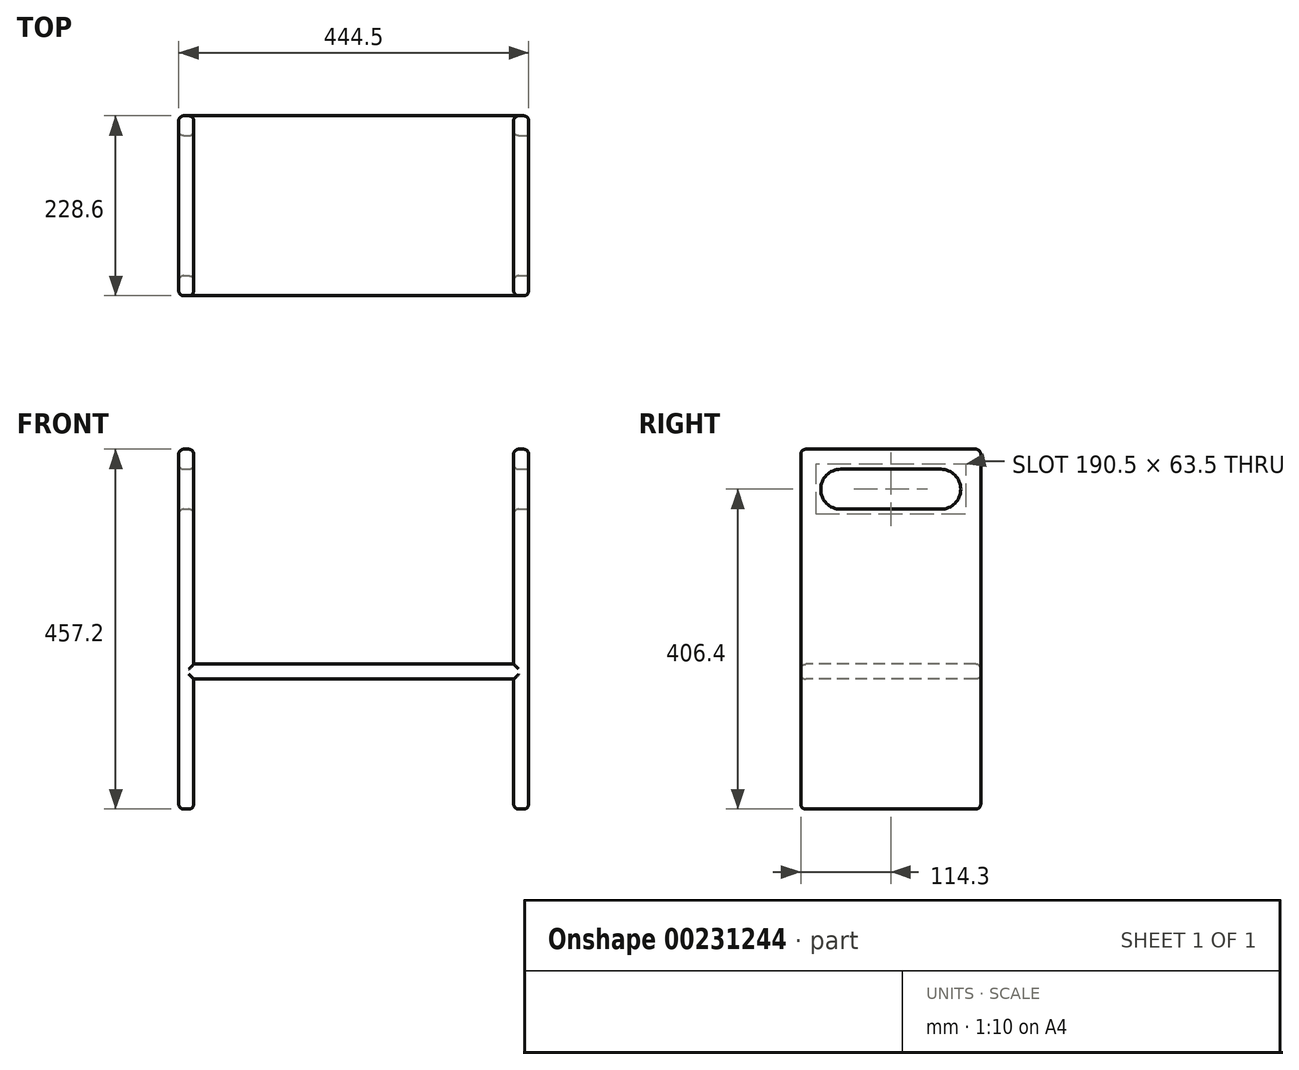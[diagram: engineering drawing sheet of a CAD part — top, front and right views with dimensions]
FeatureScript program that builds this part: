
annotation { "Feature Type Name" : "Feature", "Feature Type Description" : "" }
export const myFeature = defineFeature(function(context is Context, id is Id, definition is map)
    precondition{}
    {
        {
            var Q0;
            Q0=qCreatedBy(makeId("Top.planeOp"),FACE);
            var sketch = newSketch(context, id + "F0", { "sketchPlane" : qUnion([Q0])});
            skLineSegment(sketch, "E0.bottom", {"start": v(-209.55, 114.3) * mm, "end": v(209.55, 114.3) * mm});
            skLineSegment(sketch, "E0.top", {"start": v(-209.55, -114.3) * mm, "end": v(209.55, -114.3) * mm});
            skLineSegment(sketch, "E0.left", {"start": v(-209.55, 114.3) * mm, "end": v(-209.55, -114.3) * mm});
            skLineSegment(sketch, "E0.right", {"start": v(209.55, 114.3) * mm, "end": v(209.55, -114.3) * mm});
            skPoint(sketch, "E0.middle", {"position": v(0, 0) * mm});
            skSolve(sketch);
        }
        {
            var Q0;
            Q0 = qSketchRegion(id + "F0", true);
            extrude(context, id + "F1", {"entities" : qUnion([Q0]), "depth" : 19.05 * mm});
        }
        {
            var Q0;
            Q0=makeQuery(id+"F1.opExtrude","SWEPT_FACE",FACE,{"disambiguationData":[OSD([sQuery(id+"F0.wireOp",EDGE,"E0.top")])]});
            var sketch = newSketch(context, id + "F2", { "sketchPlane" : qUnion([Q0])});
            skLineSegment(sketch, "E1.bottom", {"start": v(203.2, -165.1) * mm, "end": v(222.25, -165.1) * mm});
            skLineSegment(sketch, "E1.top", {"start": v(203.2, 292.1) * mm, "end": v(222.25, 292.1) * mm});
            skLineSegment(sketch, "E1.left", {"start": v(203.2, -165.1) * mm, "end": v(203.2, 0) * mm});
            skLineSegment(sketch, "E1.right", {"start": v(222.25, -165.1) * mm, "end": v(222.25, 292.1) * mm});
            skPoint(sketch, "E1.middle", {"position": v(212.73, 63.5) * mm});
            skLineSegment(sketch, "E2.bottom", {"start": v(203.2, 19.05) * mm, "end": v(209.55, 19.05) * mm});
            skLineSegment(sketch, "E2.top", {"start": v(203.2, 0) * mm, "end": v(209.55, 0) * mm});
            skLineSegment(sketch, "E2.right", {"start": v(209.55, 19.05) * mm, "end": v(209.55, 0) * mm});
            skLineSegment(sketch, "E3.trimOffspring", {"start": v(203.2, 19.05) * mm, "end": v(203.2, 292.1) * mm});
            skLineSegment(sketch, "E4.MirrorCS", {"start": v(-203.2, 292.1) * mm, "end": v(-222.25, 292.1) * mm});
            skLineSegment(sketch, "E5.MirrorCS", {"start": v(-203.2, 19.05) * mm, "end": v(-203.2, 292.1) * mm});
            skLineSegment(sketch, "E6.MirrorCS", {"start": v(-222.25, -165.1) * mm, "end": v(-222.25, 292.1) * mm});
            skLineSegment(sketch, "E7.MirrorCS", {"start": v(-203.2, 19.05) * mm, "end": v(-209.55, 19.05) * mm});
            skLineSegment(sketch, "E8.MirrorCS", {"start": v(-209.55, 19.05) * mm, "end": v(-209.55, 0) * mm});
            skLineSegment(sketch, "E9.MirrorCS", {"start": v(-203.2, 0) * mm, "end": v(-209.55, 0) * mm});
            skLineSegment(sketch, "E10.MirrorCS", {"start": v(-203.2, -165.1) * mm, "end": v(-203.2, 0) * mm});
            skLineSegment(sketch, "E11.MirrorCS", {"start": v(-203.2, -165.1) * mm, "end": v(-222.25, -165.1) * mm});
            skSolve(sketch);
        }
        {
            var Q0;
            Q0 = qSketchRegion(id + "F2", true);
            var Q1;
            Q1=makeQuery(id+"F1.opExtrude","SWEPT_FACE",FACE,{"disambiguationData":[OSD([sQuery(id+"F0.wireOp",EDGE,"E0.bottom")])]});
            extrude(context, id + "F3", {"entities" : qUnion([Q0]), "operationType" : NewBodyOperationType.ADD, "endBound" : BoundingType.UP_TO_SURFACE, "oppositeDirection" : true, "endBoundEntityFace" : qUnion([Q1]), "depth" : 25.4 * mm});
        }
        {
            var Q0;
            Q0=makeQuery(id+"F3.opExtrude","SWEPT_FACE",FACE,{"disambiguationData":[OSD([sQuery(id+"F2.wireOp",EDGE,"E1.right")])]});
            var sketch = newSketch(context, id + "F4", { "sketchPlane" : qUnion([Q0])});
            skLineSegment(sketch, "E12", {"start": v(-63.5, 241.3) * mm, "end": v(63.5, 241.3) * mm, "construction": true});
            skArc(sketch, "E13", {"start": v(-63.5, 266.7) * mm, "mid": v(-88.9, 241.3) * mm, "end": v(-63.5, 215.9) * mm});
            skArc(sketch, "E14", {"start": v(63.5, 215.9) * mm, "mid": v(88.9, 241.3) * mm, "end": v(63.5, 266.7) * mm});
            skLineSegment(sketch, "E15", {"start": v(-63.5, 266.7) * mm, "end": v(63.5, 266.7) * mm});
            skLineSegment(sketch, "E16", {"start": v(-63.5, 215.9) * mm, "end": v(63.5, 215.9) * mm});
            skSolve(sketch);
        }
        {
            var Q0;
            Q0 = qSketchRegion(id + "F4", true);
            extrude(context, id + "F5", {"entities" : qUnion([Q0]), "operationType" : NewBodyOperationType.REMOVE, "endBound" : BoundingType.THROUGH_ALL, "oppositeDirection" : true, "depth" : 25.4 * mm});
        }
        {
            var Q0;
            Q0=makeQuery(id+"F5.boolean.opBoolean","COPY",EDGE,{"derivedFrom":makeQuery(id+"F5.opExtrude","CAP_EDGE",EDGE,{"disambiguationData":[OSD([sQuery(id+"F4.wireOp",EDGE,"E16")])],"isStart":true})});
            var Q1;
            Q1=makeQuery(id+"F5.boolean.opBoolean","INTERSECT",EDGE,{"derivedFrom":[makeQuery(id+"F3.opExtrude","SWEPT_FACE",FACE,{"disambiguationData":[OSD([sQuery(id+"F2.wireOp",EDGE,"E5.MirrorCS")])]}),makeQuery(id+"F5.opExtrude","SWEPT_FACE",FACE,{"disambiguationData":[OSD([sQuery(id+"F4.wireOp",EDGE,"E16")])]})]});
            var Q2;
            Q2=makeQuery(id+"F5.boolean.opBoolean","INTERSECT",EDGE,{"derivedFrom":[makeQuery(id+"F3.opExtrude","SWEPT_FACE",FACE,{"disambiguationData":[OSD([sQuery(id+"F2.wireOp",EDGE,"E3.trimOffspring")])]}),makeQuery(id+"F5.opExtrude","SWEPT_FACE",FACE,{"disambiguationData":[OSD([sQuery(id+"F4.wireOp",EDGE,"E15")])]})]});
            var Q3;
            Q3=makeQuery(id+"F5.boolean.opBoolean","INTERSECT",EDGE,{"derivedFrom":[makeQuery(id+"F3.opExtrude","SWEPT_FACE",FACE,{"disambiguationData":[OSD([sQuery(id+"F2.wireOp",EDGE,"E6.MirrorCS")])]}),makeQuery(id+"F5.opExtrude","SWEPT_FACE",FACE,{"disambiguationData":[OSD([sQuery(id+"F4.wireOp",EDGE,"E15")])]})]});
            fillet(context, id + "F6", {"entities" : qUnion([Q0, Q1, Q2, Q3]), "radius" : 6.35 * mm, "tangentPropagation" : true, "allowEdgeOverflow" : false});
        }
        {
            var Q0;
            Q0=makeQuery(id+"F3.opExtrude","CAP_EDGE",EDGE,{"disambiguationData":[OSD([sQuery(id+"F2.wireOp",EDGE,"E1.right")])],"isStart":false});
            var Q1;
            Q1=makeQuery(id+"F3.opExtrude","CAP_EDGE",EDGE,{"disambiguationData":[OSD([sQuery(id+"F2.wireOp",EDGE,"E3.trimOffspring")])],"isStart":false});
            var Q2;
            Q2=makeQuery(id+"F3.opExtrude","SWEPT_EDGE",EDGE,{"disambiguationData":[OSD([sQuery(id+"F2.wireOp",EDGE,"E1.top"),sQuery(id+"F2.wireOp",EDGE,"E1.right")])]});
            var Q3;
            Q3=makeQuery(id+"F3.opExtrude","CAP_EDGE",EDGE,{"disambiguationData":[OSD([sQuery(id+"F2.wireOp",EDGE,"E1.top")])],"isStart":false});
            var Q4;
            Q4=makeQuery(id+"F3.opExtrude","SWEPT_EDGE",EDGE,{"disambiguationData":[OSD([sQuery(id+"F2.wireOp",EDGE,"E1.top"),sQuery(id+"F2.wireOp",EDGE,"E3.trimOffspring")])]});
            var Q5;
            Q5=makeQuery(id+"F3.opExtrude","CAP_EDGE",EDGE,{"disambiguationData":[OSD([sQuery(id+"F2.wireOp",EDGE,"E1.top")])],"isStart":true});
            var Q6;
            Q6=makeQuery(id+"F3.opExtrude","CAP_EDGE",EDGE,{"disambiguationData":[OSD([sQuery(id+"F2.wireOp",EDGE,"E1.right")])],"isStart":true});
            var Q7;
            Q7=makeQuery(id+"F3.opExtrude","CAP_EDGE",EDGE,{"disambiguationData":[OSD([sQuery(id+"F2.wireOp",EDGE,"E3.trimOffspring")])],"isStart":true});
            var Q8;
            Q8=makeQuery(id+"F3.opExtrude","CAP_EDGE",EDGE,{"disambiguationData":[OSD([sQuery(id+"F2.wireOp",EDGE,"E1.bottom")])],"isStart":false});
            var Q9;
            Q9=makeQuery(id+"F3.opExtrude","CAP_EDGE",EDGE,{"disambiguationData":[OSD([sQuery(id+"F2.wireOp",EDGE,"E1.left")])],"isStart":false});
            var Q10;
            Q10=makeQuery(id+"F3.opExtrude","SWEPT_EDGE",EDGE,{"disambiguationData":[OSD([sQuery(id+"F2.wireOp",EDGE,"E1.bottom"),sQuery(id+"F2.wireOp",EDGE,"E1.left")])]});
            var Q11;
            Q11=makeQuery(id+"F3.opExtrude","SWEPT_EDGE",EDGE,{"disambiguationData":[OSD([sQuery(id+"F2.wireOp",EDGE,"E1.bottom"),sQuery(id+"F2.wireOp",EDGE,"E1.right")])]});
            var Q12;
            Q12=makeQuery(id+"F3.opExtrude","CAP_EDGE",EDGE,{"disambiguationData":[OSD([sQuery(id+"F2.wireOp",EDGE,"E1.bottom")])],"isStart":true});
            var Q13;
            Q13=makeQuery(id+"F3.opExtrude","CAP_EDGE",EDGE,{"disambiguationData":[OSD([sQuery(id+"F2.wireOp",EDGE,"E1.left")])],"isStart":true});
            fillet(context, id + "F7", {"entities" : qUnion([Q0, Q1, Q2, Q3, Q4, Q5, Q6, Q7, Q8, Q9, Q10, Q11, Q12, Q13]), "radius" : 6.35 * mm, "tangentPropagation" : true, "allowEdgeOverflow" : false});
        }
        {
            var Q0;
            Q0=makeQuery(id+"F3.opExtrude","CAP_EDGE",EDGE,{"disambiguationData":[OSD([sQuery(id+"F2.wireOp",EDGE,"E5.MirrorCS")])],"isStart":false});
            var Q1;
            Q1=makeQuery(id+"F3.opExtrude","CAP_EDGE",EDGE,{"disambiguationData":[OSD([sQuery(id+"F2.wireOp",EDGE,"E4.MirrorCS")])],"isStart":false});
            var Q2;
            Q2=makeQuery(id+"F3.opExtrude","CAP_EDGE",EDGE,{"disambiguationData":[OSD([sQuery(id+"F2.wireOp",EDGE,"E6.MirrorCS")])],"isStart":false});
            var Q3;
            Q3=makeQuery(id+"F3.opExtrude","SWEPT_EDGE",EDGE,{"disambiguationData":[OSD([sQuery(id+"F2.wireOp",EDGE,"E4.MirrorCS"),sQuery(id+"F2.wireOp",EDGE,"E5.MirrorCS")])]});
            var Q4;
            Q4=makeQuery(id+"F3.opExtrude","SWEPT_EDGE",EDGE,{"disambiguationData":[OSD([sQuery(id+"F2.wireOp",EDGE,"E4.MirrorCS"),sQuery(id+"F2.wireOp",EDGE,"E6.MirrorCS")])]});
            var Q5;
            Q5=makeQuery(id+"F3.opExtrude","CAP_EDGE",EDGE,{"disambiguationData":[OSD([sQuery(id+"F2.wireOp",EDGE,"E4.MirrorCS")])],"isStart":true});
            var Q6;
            Q6=makeQuery(id+"F3.opExtrude","CAP_EDGE",EDGE,{"disambiguationData":[OSD([sQuery(id+"F2.wireOp",EDGE,"E5.MirrorCS")])],"isStart":true});
            var Q7;
            Q7=makeQuery(id+"F3.opExtrude","CAP_EDGE",EDGE,{"disambiguationData":[OSD([sQuery(id+"F2.wireOp",EDGE,"E6.MirrorCS")])],"isStart":true});
            var Q8;
            Q8=makeQuery(id+"F3.opExtrude","CAP_EDGE",EDGE,{"disambiguationData":[OSD([sQuery(id+"F2.wireOp",EDGE,"E10.MirrorCS")])],"isStart":true});
            var Q9;
            Q9=makeQuery(id+"F3.opExtrude","CAP_EDGE",EDGE,{"disambiguationData":[OSD([sQuery(id+"F2.wireOp",EDGE,"E11.MirrorCS")])],"isStart":true});
            var Q10;
            Q10=makeQuery(id+"F3.opExtrude","SWEPT_EDGE",EDGE,{"disambiguationData":[OSD([sQuery(id+"F2.wireOp",EDGE,"E10.MirrorCS"),sQuery(id+"F2.wireOp",EDGE,"E11.MirrorCS")])]});
            var Q11;
            Q11=makeQuery(id+"F3.opExtrude","SWEPT_EDGE",EDGE,{"disambiguationData":[OSD([sQuery(id+"F2.wireOp",EDGE,"E6.MirrorCS"),sQuery(id+"F2.wireOp",EDGE,"E11.MirrorCS")])]});
            var Q12;
            Q12=makeQuery(id+"F3.opExtrude","CAP_EDGE",EDGE,{"disambiguationData":[OSD([sQuery(id+"F2.wireOp",EDGE,"E11.MirrorCS")])],"isStart":false});
            var Q13;
            Q13=makeQuery(id+"F3.opExtrude","CAP_EDGE",EDGE,{"disambiguationData":[OSD([sQuery(id+"F2.wireOp",EDGE,"E10.MirrorCS")])],"isStart":false});
            fillet(context, id + "F8", {"entities" : qUnion([Q0, Q1, Q2, Q3, Q4, Q5, Q6, Q7, Q8, Q9, Q10, Q11, Q12, Q13]), "radius" : 6.35 * mm, "tangentPropagation" : true, "allowEdgeOverflow" : false});
        }
        {
            var Q0;
            Q0=makeQuery(id+"F1.opExtrude","CAP_EDGE",EDGE,{"disambiguationData":[OSD([sQuery(id+"F0.wireOp",EDGE,"E0.bottom")])],"isStart":false});
            var Q1;
            Q1=makeQuery(id+"F1.opExtrude","CAP_EDGE",EDGE,{"disambiguationData":[OSD([sQuery(id+"F0.wireOp",EDGE,"E0.bottom")])],"isStart":true});
            var Q2;
            Q2=makeQuery(id+"F1.opExtrude","CAP_EDGE",EDGE,{"disambiguationData":[OSD([sQuery(id+"F0.wireOp",EDGE,"E0.top")])],"isStart":false});
            var Q3;
            Q3=makeQuery(id+"F1.opExtrude","CAP_EDGE",EDGE,{"disambiguationData":[OSD([sQuery(id+"F0.wireOp",EDGE,"E0.top")])],"isStart":true});
            fillet(context, id + "F9", {"entities" : qUnion([Q0, Q1, Q2, Q3]), "radius" : 6.35 * mm, "tangentPropagation" : true, "allowEdgeOverflow" : false});
        }
    });
